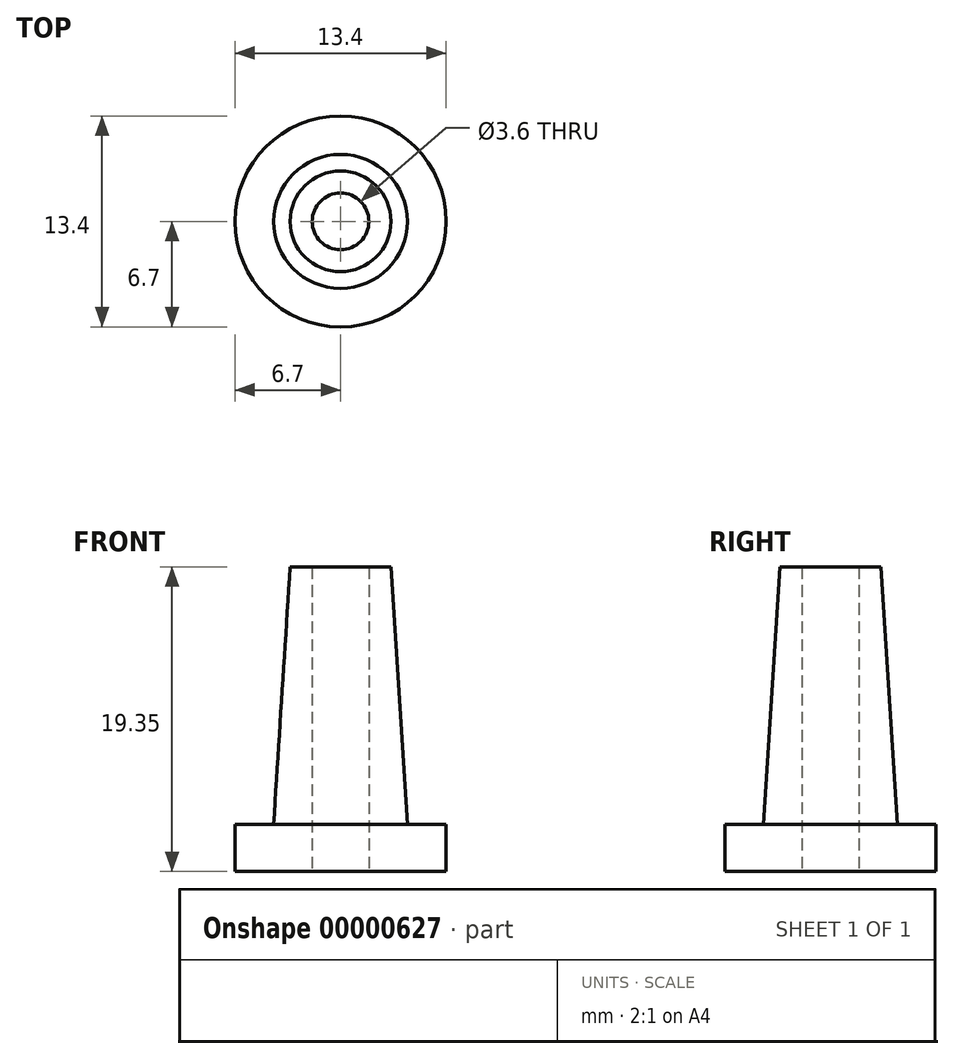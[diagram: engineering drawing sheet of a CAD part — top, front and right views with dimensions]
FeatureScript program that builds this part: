
annotation { "Feature Type Name" : "Feature", "Feature Type Description" : "" }
export const myFeature = defineFeature(function(context is Context, id is Id, definition is map)
    precondition{}
    {
        {
            var Q0;
            Q0=qCreatedBy(makeId("Front.planeOp"),FACE);
            var sketch = newSketch(context, id + "F0", { "sketchPlane" : qUnion([Q0])});
            skLineSegment(sketch, "E0", {"start": v(-1.8, 0) * mm, "end": v(-6.7, 0) * mm});
            skLineSegment(sketch, "E1", {"start": v(-6.7, 0) * mm, "end": v(-6.7, 3) * mm});
            skLineSegment(sketch, "E2", {"start": v(-6.7, 3) * mm, "end": v(-4.25, 3) * mm});
            skLineSegment(sketch, "E3", {"start": v(-4.25, 3) * mm, "end": v(-3.2, 19.35) * mm});
            skLineSegment(sketch, "E4", {"start": v(-3.2, 19.35) * mm, "end": v(-1.8, 19.35) * mm});
            skLineSegment(sketch, "E5", {"start": v(-1.8, 19.35) * mm, "end": v(-1.8, 0) * mm});
            skLineSegment(sketch, "E6", {"start": v(0, 0) * mm, "end": v(0, 43.24) * mm, "construction": true});
            skSolve(sketch);
        }
        {
            var Q0;
            Q0=makeQuery(id+"F0.imprint","IMPRINT",FACE,{"disambiguationData":[TD([[makeQuery(id+"F0.imprint","IMPRINT",EDGE,{"derivedFrom":sQuery(id+"F0.wireOp",EDGE,"E0")}),-1.0]])]});
            var Q1;
            Q1=sQuery(id+"F0.wireOp",EDGE,"E6");
            revolve(context, id + "F1", {"entities" : qUnion([Q0]), "axis" : qUnion([Q1]), "revolveType" : RevolveType.FULL});
        }
        {
            var Q0;
            Q0=makeQuery(id+"F0.imprint","IMPRINT",FACE,{"disambiguationData":[TD([[makeQuery(id+"F0.imprint","IMPRINT",EDGE,{"derivedFrom":sQuery(id+"F0.wireOp",EDGE,"E0")}),-1.0]])]});
            var Q1;
            Q1=sQuery(id+"F0.wireOp",EDGE,"E6");
            revolve(context, id + "F2", {"operationType" : NewBodyOperationType.ADD, "entities" : qUnion([Q0]), "axis" : qUnion([Q1]), "revolveType" : RevolveType.FULL});
        }
    });
